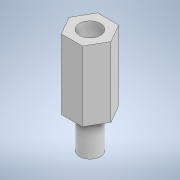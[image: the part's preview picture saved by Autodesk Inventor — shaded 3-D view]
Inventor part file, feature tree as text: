
AUTODESK INVENTOR PART (.ipt)
format: ipt  version: 2022 (Build 260153000, 153)  size: 110,592 bytes
history: native  units: mm
features: sketch x4, extrude x3
ambient origin geometry x8: Origin, YZ Plane, XZ Plane, XY Plane, X Axis, Y Axis, Z Axis, Center Point
bodies: Solid1 (feature_tree)
feature tree (7):
  sketch  "Sketch1"  dims[d0=6.0mm d1=10.0mm d2=0.0mm]
  sketch  "Sketch2"  dims[d3=3.0mm d4=3.0mm]
  extrude  "Extrusion1"  Depth=10.0mm TaperAngle=0.0deg
  sketch  "Sketch3"  dims[d5=5.0mm d6=0.0mm d7=10.0mm d8=0.0mm]
  sketch  "Sketch4"
  extrude  "Extrusion2"  Depth=3.0mm
  extrude  "Extrusion3"  Depth=10.0mm TaperAngle=0.0deg
